# Revit family: SCLT-CM
name_source: partatom
category: Lighting Fixtures
revit_build: Autodesk Revit 2014 (Build: 20130308_1515(x64)
units: mm (PartAtom-declared; Revit-internal decimal feet)

## types (3) — shared parameters
Cable Height = 24"
Color Filter = 16777215
Default Elevation = 48"
Description = LED Troffer with Advanced Solid State Technology
Dimming Lamp Color Temperature Shift = Incandescent Lamp Curve
Emit Shape Visible in Rendering = No
Finish = Hubbell-Arctic White
Glass = Hubbell - White Glass
Lamp = LED
Load Classification = Lighting
Manufacturer = Hubbell Lighting
Model = SCLT
Photometric Notes = More IES files download Photometric Web Link
Photometric Web File = generic.ies
Power Factor = 1
Product Documentation Link = https://hubbellcdn.com
Product Page Link = https://www.hubbell.com
Tilt Angle = 90.00°
URL = https://www.hubbell.com
Voltage = 120 V
Warranty = 5 Years Limited Warranty

## per-type parameters (varying)
| type | Apparent Load | Emit from Rectangle Length | Emit from Rectangle Width | Size Option | Wattage Comments | Watts | zz Width 1 |
| SCLT-24 | 38 VA | 47" | 23" | SCLT : 24 | 34W | 38 W | 48" |
| SCLT-22 | 38 VA | 23" | 23" | SCLT : 22 | 28W | 38 W | 24" |
| SCLT-14 | 45 VA | 47" | 11" | SCLT : 14 | 45W | 45 W | 48" |

## geometry (parser evidence)
native form markers: Blend x3, Sweep x2
no freeform markers — native parametric forms only
